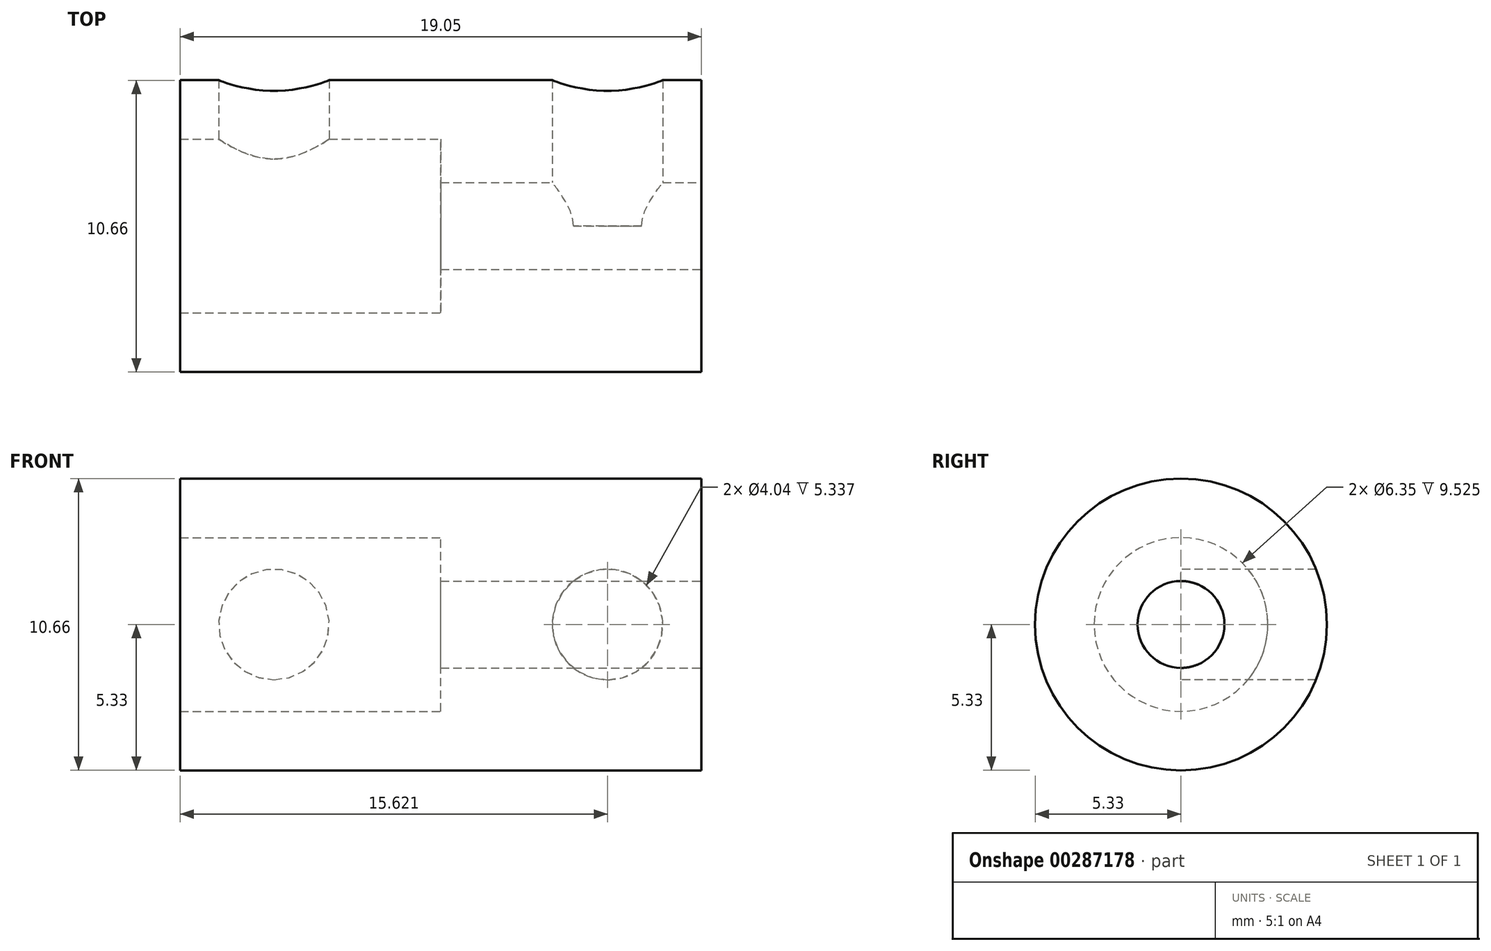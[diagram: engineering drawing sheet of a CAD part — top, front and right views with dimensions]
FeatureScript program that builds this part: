
annotation { "Feature Type Name" : "Feature", "Feature Type Description" : "" }
export const myFeature = defineFeature(function(context is Context, id is Id, definition is map)
    precondition{}
    {
        {
            var Q0;
            Q0=qCreatedBy(makeId("Front.planeOp"),FACE);
            var sketch = newSketch(context, id + "F0", { "sketchPlane" : qUnion([Q0])});
            skLineSegment(sketch, "E0", {"start": v(0, 0) * mm, "end": v(-19.34, 0) * mm, "construction": true});
            skLineSegment(sketch, "E1.bottom", {"start": v(-19.05, 5.33) * mm, "end": v(-9.53, 5.33) * mm});
            skLineSegment(sketch, "E1.top", {"start": v(-19.05, 3.17) * mm, "end": v(-9.52, 3.18) * mm});
            skLineSegment(sketch, "E1.left", {"start": v(-19.05, 5.33) * mm, "end": v(-19.05, 3.18) * mm});
            skLineSegment(sketch, "E1.right", {"start": v(-9.53, 5.33) * mm, "end": v(-9.53, 3.18) * mm});
            skLineSegment(sketch, "E2.bottom", {"start": v(-9.53, 5.33) * mm, "end": v(0, 5.33) * mm});
            skLineSegment(sketch, "E2.top", {"start": v(-9.52, 1.59) * mm, "end": v(0, 1.59) * mm});
            skLineSegment(sketch, "E2.left", {"start": v(-9.53, 5.33) * mm, "end": v(-9.53, 1.59) * mm});
            skLineSegment(sketch, "E2.right", {"start": v(0, 5.33) * mm, "end": v(0, 1.59) * mm});
            skLineSegment(sketch, "E3.MirrorCS", {"start": v(-9.53, -5.33) * mm, "end": v(-9.53, -3.18) * mm});
            skLineSegment(sketch, "E4.MirrorCS", {"start": v(0, -5.33) * mm, "end": v(0, -1.59) * mm});
            skLineSegment(sketch, "E5.MirrorCS", {"start": v(-9.53, -5.33) * mm, "end": v(-9.53, -1.59) * mm});
            skLineSegment(sketch, "E6.MirrorCS", {"start": v(-9.52, -1.59) * mm, "end": v(0, -1.59) * mm});
            skLineSegment(sketch, "E7.MirrorCS", {"start": v(-9.53, -5.33) * mm, "end": v(0, -5.33) * mm});
            skLineSegment(sketch, "E8.MirrorCS", {"start": v(-19.05, -5.33) * mm, "end": v(-19.05, -3.18) * mm});
            skLineSegment(sketch, "E9.MirrorCS", {"start": v(-19.05, -3.18) * mm, "end": v(-9.52, -3.18) * mm});
            skLineSegment(sketch, "E10.MirrorCS", {"start": v(-19.05, -5.33) * mm, "end": v(-9.53, -5.33) * mm});
            skSolve(sketch);
        }
        {
            var Q0;
            Q0 = qSketchRegion(id + "F0", true);
            var Q1;
            Q1=sQuery(id+"F0.wireOp",EDGE,"E0");
            revolve(context, id + "F1", {"entities" : qUnion([Q0]), "axis" : qUnion([Q1]), "revolveType" : RevolveType.FULL});
        }
        {
            var Q0;
            Q0=qCreatedBy(makeId("Front.planeOp"),FACE);
            var sketch = newSketch(context, id + "F2", { "sketchPlane" : qUnion([Q0])});
            skLineSegment(sketch, "E11", {"start": v(0, 0) * mm, "end": v(-17.33, 0) * mm, "construction": true});
            skCircle(sketch, "E12", {"center": v(-15.62, 0) * mm, "radius": 2.02 * mm});
            skCircle(sketch, "E13", {"center": v(-3.43, 0) * mm, "radius": 2.02 * mm});
            skSolve(sketch);
        }
        {
            var Q0;
            Q0 = qSketchRegion(id + "F2", true);
            extrude(context, id + "F3", {"entities" : qUnion([Q0]), "operationType" : NewBodyOperationType.REMOVE, "oppositeDirection" : true, "depth" : 6.25 * mm});
        }
    });
